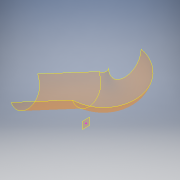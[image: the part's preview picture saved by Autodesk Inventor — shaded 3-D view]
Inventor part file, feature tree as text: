
AUTODESK INVENTOR PART (.ipt)
format: ipt  version: 2016 (Build 200138000, 138)  size: 142,848 bytes
history: native  units: in
note: dims shown in document units (in); Inventor stores cm internally (conversion verified against a paired STEP export)
features: plane x2, sketch x2, other x1, sweep x1
ambient origin geometry x8: Origin, YZ Plane, XZ Plane, XY Plane, X Axis, Y Axis, Z Axis, Center Point
bodies: Body1 (feature_tree)
feature tree (6):
  plane  "Work Plane8"
  plane  "Work Plane13"
  sketch  "Sketch9"  dims[d18=4.0in d19=4.0in d26=2.75in d33=0.0in d34=0.0in]
  sketch  "3D Sketch1"
  other  "Srf1"
  sweep  "SweepSrf1"
